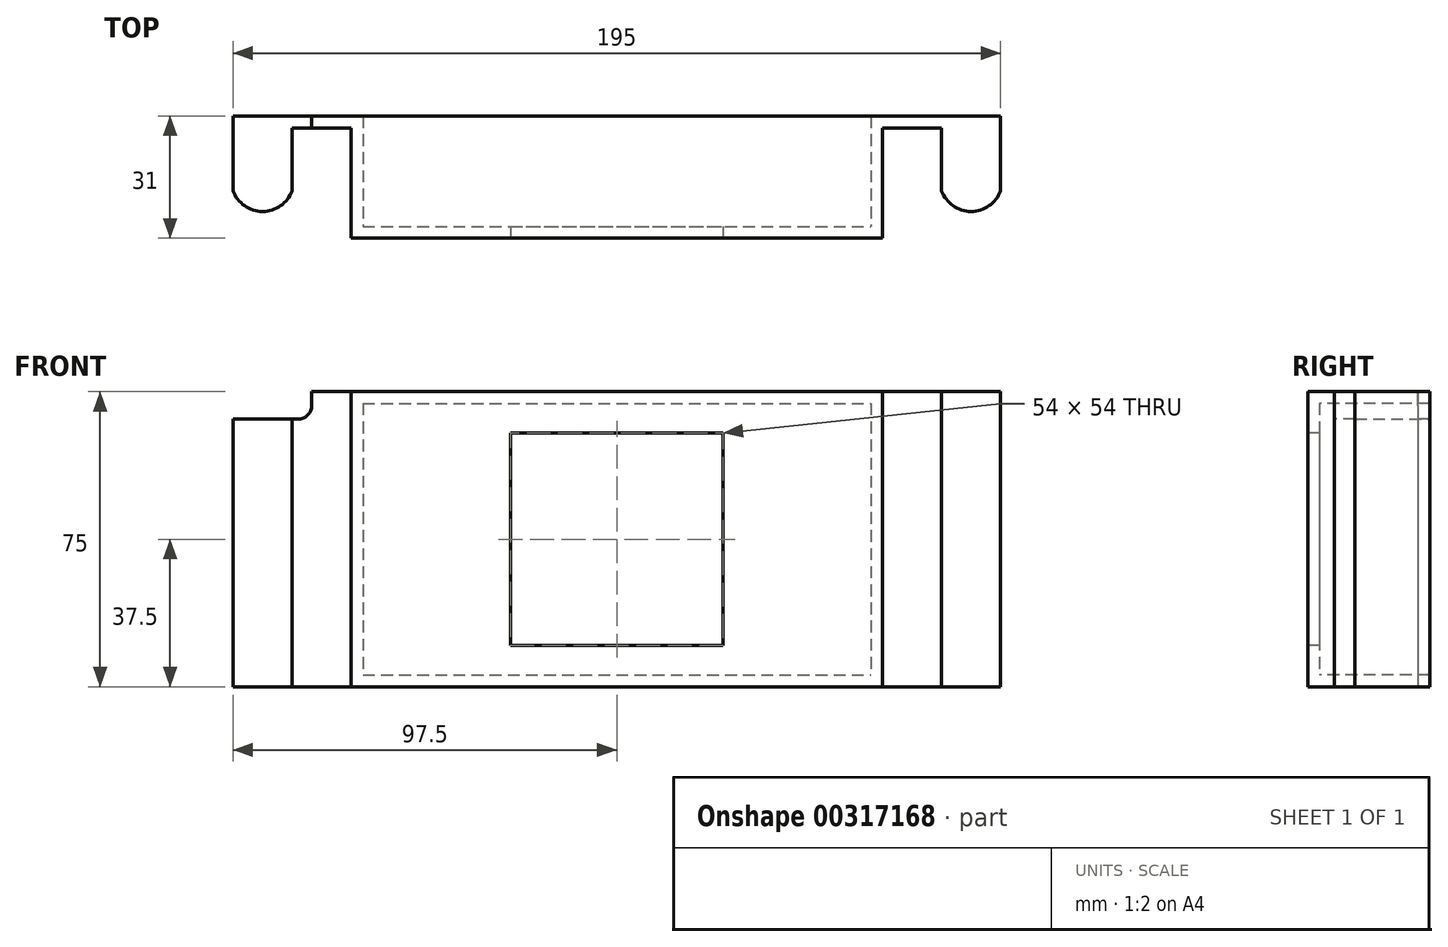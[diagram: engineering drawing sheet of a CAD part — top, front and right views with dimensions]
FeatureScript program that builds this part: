
annotation { "Feature Type Name" : "Feature", "Feature Type Description" : "" }
export const myFeature = defineFeature(function(context is Context, id is Id, definition is map)
    precondition{}
    {
        {
            var Q0;
            Q0=qCreatedBy(makeId("Front.planeOp"),FACE);
            var sketch = newSketch(context, id + "F0", { "sketchPlane" : qUnion([Q0])});
            skLineSegment(sketch, "E0.bottom", {"start": v(30, 30) * mm, "end": v(-30, 30) * mm});
            skLineSegment(sketch, "E0.top", {"start": v(30, -30) * mm, "end": v(-30, -30) * mm});
            skLineSegment(sketch, "E0.left", {"start": v(30, 30) * mm, "end": v(30, -30) * mm});
            skLineSegment(sketch, "E0.right", {"start": v(-30, 30) * mm, "end": v(-30, -30) * mm});
            skPoint(sketch, "E0.middle", {"position": v(0, 0) * mm});
            skCircle(sketch, "E1", {"center": v(0, 0) * mm, "radius": 22.4 * mm});
            skSolve(sketch);
        }
        {
            var Q0;
            Q0=qSketchRegion(id+"F0",true);
            extrude(context, id + "F1", {"entities" : qUnion([Q0]), "depth" : 3 * mm});
        }
        {
            var Q0;
            Q0=makeQuery(id+"F1.opExtrude","CAP_FACE",FACE,{"disambiguationData":[OSD([sQuery(id+"F0.wireOp",EDGE,"E0.bottom"),sQuery(id+"F0.wireOp",EDGE,"E0.top"),sQuery(id+"F0.wireOp",EDGE,"E0.left"),sQuery(id+"F0.wireOp",EDGE,"E0.right"),sQuery(id+"F0.wireOp",EDGE,"E1")])],"isStart":true});
            var sketch = newSketch(context, id + "F2", { "sketchPlane" : qUnion([Q0])});
            skLineSegment(sketch, "E2.bottom", {"start": v(30, 30) * mm, "end": v(-30, 30) * mm});
            skLineSegment(sketch, "E2.top", {"start": v(30, -30) * mm, "end": v(-30, -30) * mm});
            skLineSegment(sketch, "E2.left", {"start": v(30, 30) * mm, "end": v(30, -30) * mm});
            skLineSegment(sketch, "E2.right", {"start": v(-30, 30) * mm, "end": v(-30, -30) * mm});
            skPoint(sketch, "E2.middle", {"position": v(0, 0) * mm});
            skLineSegment(sketch, "E3.bottom", {"start": v(27, 27) * mm, "end": v(-27, 27) * mm});
            skLineSegment(sketch, "E3.top", {"start": v(27, -27) * mm, "end": v(-27, -27) * mm});
            skLineSegment(sketch, "E3.left", {"start": v(27, 27) * mm, "end": v(27, -27) * mm});
            skLineSegment(sketch, "E3.right", {"start": v(-27, 27) * mm, "end": v(-27, -27) * mm});
            skSolve(sketch);
        }
        {
            var Q0;
            Q0=qSketchRegion(id+"F2",true);
            extrude(context, id + "F3", {"entities" : qUnion([Q0]), "operationType" : NewBodyOperationType.ADD, "depth" : 15 * mm});
        }
        {
            var Q0;
            Q0=makeQuery(id+"F3.opExtrude","CAP_FACE",FACE,{"disambiguationData":[OSD([sQuery(id+"F2.wireOp",EDGE,"E2.bottom"),sQuery(id+"F2.wireOp",EDGE,"E2.top"),sQuery(id+"F2.wireOp",EDGE,"E2.left"),sQuery(id+"F2.wireOp",EDGE,"E2.right"),sQuery(id+"F2.wireOp",EDGE,"E3.bottom"),sQuery(id+"F2.wireOp",EDGE,"E3.top"),sQuery(id+"F2.wireOp",EDGE,"E3.left"),sQuery(id+"F2.wireOp",EDGE,"E3.right")])],"isStart":false});
            var sketch = newSketch(context, id + "F4", { "sketchPlane" : qUnion([Q0])});
            skLineSegment(sketch, "E4.bottom", {"start": v(67.5, 37.5) * mm, "end": v(-67.5, 37.5) * mm});
            skLineSegment(sketch, "E4.top", {"start": v(67.5, -37.5) * mm, "end": v(-67.5, -37.5) * mm});
            skLineSegment(sketch, "E4.left", {"start": v(67.5, 37.5) * mm, "end": v(67.5, -37.5) * mm});
            skLineSegment(sketch, "E4.right", {"start": v(-67.5, 37.5) * mm, "end": v(-67.5, -37.5) * mm});
            skPoint(sketch, "E4.middle", {"position": v(0, 0) * mm});
            skLineSegment(sketch, "E5.bottom", {"start": v(27, 27) * mm, "end": v(-27, 27) * mm});
            skLineSegment(sketch, "E5.top", {"start": v(27, -27) * mm, "end": v(-27, -27) * mm});
            skLineSegment(sketch, "E5.left", {"start": v(27, 27) * mm, "end": v(27, -27) * mm});
            skLineSegment(sketch, "E5.right", {"start": v(-27, 27) * mm, "end": v(-27, -27) * mm});
            skSolve(sketch);
        }
        {
            var Q0;
            Q0=qSketchRegion(id+"F4",true);
            extrude(context, id + "F5", {"entities" : qUnion([Q0]), "operationType" : NewBodyOperationType.ADD, "depth" : 3 * mm});
        }
        {
            var Q0;
            Q0=makeQuery(id+"F5.opExtrude","CAP_FACE",FACE,{"disambiguationData":[OSD([sQuery(id+"F4.wireOp",EDGE,"E4.bottom"),sQuery(id+"F4.wireOp",EDGE,"E4.top"),sQuery(id+"F4.wireOp",EDGE,"E4.left"),sQuery(id+"F4.wireOp",EDGE,"E4.right"),sQuery(id+"F4.wireOp",EDGE,"E5.bottom"),sQuery(id+"F4.wireOp",EDGE,"E5.top"),sQuery(id+"F4.wireOp",EDGE,"E5.left"),sQuery(id+"F4.wireOp",EDGE,"E5.right")])],"isStart":false});
            var sketch = newSketch(context, id + "F6", { "sketchPlane" : qUnion([Q0])});
            skLineSegment(sketch, "E6.bottom", {"start": v(67.5, 37.5) * mm, "end": v(-67.5, 37.5) * mm});
            skLineSegment(sketch, "E6.top", {"start": v(67.5, -37.5) * mm, "end": v(-67.5, -37.5) * mm});
            skLineSegment(sketch, "E6.left", {"start": v(67.5, 37.5) * mm, "end": v(67.5, -37.5) * mm});
            skLineSegment(sketch, "E6.right", {"start": v(-67.5, 37.5) * mm, "end": v(-67.5, -37.5) * mm});
            skPoint(sketch, "E6.middle", {"position": v(0, 0) * mm});
            skLineSegment(sketch, "E7.bottom", {"start": v(64.5, 34.5) * mm, "end": v(-64.5, 34.5) * mm});
            skLineSegment(sketch, "E7.top", {"start": v(64.5, -34.5) * mm, "end": v(-64.5, -34.5) * mm});
            skLineSegment(sketch, "E7.left", {"start": v(64.5, 34.5) * mm, "end": v(64.5, -34.5) * mm});
            skLineSegment(sketch, "E7.right", {"start": v(-64.5, 34.5) * mm, "end": v(-64.5, -34.5) * mm});
            skSolve(sketch);
        }
        {
            var Q0;
            Q0=qSketchRegion(id+"F6",true);
            extrude(context, id + "F7", {"entities" : qUnion([Q0]), "operationType" : NewBodyOperationType.ADD, "depth" : 25 * mm});
        }
        {
            var Q0;
            Q0=makeQuery(id+"F7.opExtrude","CAP_FACE",FACE,{"disambiguationData":[OSD([sQuery(id+"F6.wireOp",EDGE,"E6.bottom"),sQuery(id+"F6.wireOp",EDGE,"E6.top"),sQuery(id+"F6.wireOp",EDGE,"E6.left"),sQuery(id+"F6.wireOp",EDGE,"E6.right"),sQuery(id+"F6.wireOp",EDGE,"E7.bottom"),sQuery(id+"F6.wireOp",EDGE,"E7.top"),sQuery(id+"F6.wireOp",EDGE,"E7.left"),sQuery(id+"F6.wireOp",EDGE,"E7.right")])],"isStart":false});
            var sketch = newSketch(context, id + "F8", { "sketchPlane" : qUnion([Q0])});
            skLineSegment(sketch, "E8.bottom", {"start": v(97.5, 37.5) * mm, "end": v(-97.5, 37.5) * mm});
            skLineSegment(sketch, "E8.top", {"start": v(97.5, -37.5) * mm, "end": v(-97.5, -37.5) * mm});
            skLineSegment(sketch, "E8.left", {"start": v(97.5, 37.5) * mm, "end": v(97.5, -37.5) * mm});
            skLineSegment(sketch, "E8.right", {"start": v(-97.5, 37.5) * mm, "end": v(-97.5, -37.5) * mm});
            skPoint(sketch, "E8.middle", {"position": v(0, 0) * mm});
            skLineSegment(sketch, "E9.bottom", {"start": v(64.5, 34.5) * mm, "end": v(-64.5, 34.5) * mm});
            skLineSegment(sketch, "E9.top", {"start": v(64.5, -34.5) * mm, "end": v(-64.5, -34.5) * mm});
            skLineSegment(sketch, "E9.left", {"start": v(64.5, 34.5) * mm, "end": v(64.5, -34.5) * mm});
            skLineSegment(sketch, "E9.right", {"start": v(-64.5, 34.5) * mm, "end": v(-64.5, -34.5) * mm});
            skSolve(sketch);
        }
        {
            var Q0;
            Q0=qSketchRegion(id+"F8",true);
            extrude(context, id + "F9", {"entities" : qUnion([Q0]), "operationType" : NewBodyOperationType.ADD, "depth" : 3 * mm});
        }
        {
            var Q0;
            {var subQ0=sQuery(id+"F8.wireOp",EDGE,"E8.left");var subQ1=sQuery(id+"F8.wireOp",EDGE,"E8.bottom");var subQ2=sQuery(id+"F8.wireOp",EDGE,"E8.top");Q0=makeQuery(id+"F9.boolean.opBoolean","SPLIT",FACE,{"disambiguationData":[TD([makeQuery(id+"F5.opExtrude","SWEPT_FACE",FACE,{"disambiguationData":[OSD([sQuery(id+"F4.wireOp",EDGE,"E4.left")])]})])],"derivedFrom":makeQuery(id+"F9.opExtrude","CAP_FACE",FACE,{"disambiguationData":[OSD([subQ1,subQ2,subQ0,sQuery(id+"F8.wireOp",EDGE,"E8.right"),sQuery(id+"F8.wireOp",EDGE,"E9.bottom"),sQuery(id+"F8.wireOp",EDGE,"E9.top"),sQuery(id+"F8.wireOp",EDGE,"E9.left"),sQuery(id+"F8.wireOp",EDGE,"E9.right")])],"isStart":true})});}
            var sketch = newSketch(context, id + "F10", { "sketchPlane" : qUnion([Q0])});
            skLineSegment(sketch, "E10.top", {"start": v(-97.5, -37.5) * mm, "end": v(-82.5, -37.5) * mm});
            skLineSegment(sketch, "E11", {"start": v(-97.5, 30.5) * mm, "end": v(-82.5, 30.5) * mm});
            skLineSegment(sketch, "E12", {"start": v(-82.5, 30.5) * mm, "end": v(-82.5, -37.5) * mm});
            skLineSegment(sketch, "E13", {"start": v(-97.5, -37.5) * mm, "end": v(-97.5, 30.5) * mm});
            skSolve(sketch);
        }
        {
            var Q0;
            Q0=qSketchRegion(id+"F10",true);
            extrude(context, id + "F11", {"entities" : qUnion([Q0]), "operationType" : NewBodyOperationType.ADD, "depth" : 25 * mm});
        }
        {
            var Q0;
            {var subQ0=sQuery(id+"F8.wireOp",EDGE,"E8.bottom");var subQ1=sQuery(id+"F8.wireOp",EDGE,"E8.top");var subQ2=sQuery(id+"F8.wireOp",EDGE,"E8.right");Q0=makeQuery(id+"F9.boolean.opBoolean","SPLIT",FACE,{"disambiguationData":[TD([makeQuery(id+"F5.opExtrude","SWEPT_FACE",FACE,{"disambiguationData":[OSD([sQuery(id+"F4.wireOp",EDGE,"E4.right")])]})])],"derivedFrom":makeQuery(id+"F9.opExtrude","CAP_FACE",FACE,{"disambiguationData":[OSD([subQ0,subQ1,sQuery(id+"F8.wireOp",EDGE,"E8.left"),subQ2,sQuery(id+"F8.wireOp",EDGE,"E9.bottom"),sQuery(id+"F8.wireOp",EDGE,"E9.top"),sQuery(id+"F8.wireOp",EDGE,"E9.left"),sQuery(id+"F8.wireOp",EDGE,"E9.right")])],"isStart":true})});}
            var sketch = newSketch(context, id + "F12", { "sketchPlane" : qUnion([Q0])});
            skLineSegment(sketch, "E14.bottom", {"start": v(97.5, 37.5) * mm, "end": v(82.5, 37.5) * mm});
            skLineSegment(sketch, "E14.top", {"start": v(97.5, -37.5) * mm, "end": v(82.5, -37.5) * mm});
            skLineSegment(sketch, "E14.left", {"start": v(97.5, 37.5) * mm, "end": v(97.5, -37.5) * mm});
            skLineSegment(sketch, "E14.right", {"start": v(82.5, 37.5) * mm, "end": v(82.5, -37.5) * mm});
            skSolve(sketch);
        }
        {
            var Q0;
            Q0=qSketchRegion(id+"F12",true);
            extrude(context, id + "F13", {"entities" : qUnion([Q0]), "operationType" : NewBodyOperationType.ADD, "depth" : 25 * mm});
        }
        {
            var Q0;
            Q0=makeQuery(id+"F13.boolean.opBoolean","MERGE",FACE,{"derivedFrom":[makeQuery(id+"F11.boolean.opBoolean","MERGE",FACE,{"derivedFrom":[makeQuery(id+"F9.boolean.opBoolean","MERGE",FACE,{"derivedFrom":[makeQuery(id+"F7.boolean.opBoolean","MERGE",FACE,{"derivedFrom":[makeQuery(id+"F5.opExtrude","SWEPT_FACE",FACE,{"disambiguationData":[OSD([sQuery(id+"F4.wireOp",EDGE,"E4.bottom")])]}),makeQuery(id+"F7.opExtrude","SWEPT_FACE",FACE,{"disambiguationData":[OSD([sQuery(id+"F6.wireOp",EDGE,"E6.bottom")])]})]}),makeQuery(id+"F9.opExtrude","SWEPT_FACE",FACE,{"disambiguationData":[OSD([sQuery(id+"F8.wireOp",EDGE,"E8.bottom")])]})]}),makeQuery(id+"F11.opExtrude","SWEPT_FACE",FACE,{"disambiguationData":[OSD([sQuery(id+"F10.wireOp",EDGE,"E10.bottom")])]})]}),makeQuery(id+"F13.opExtrude","SWEPT_FACE",FACE,{"disambiguationData":[OSD([sQuery(id+"F12.wireOp",EDGE,"E14.bottom")])]})]});
            var sketch = newSketch(context, id + "F14", { "sketchPlane" : qUnion([Q0])});
            skArc(sketch, "E15", {"start": v(-97.5, 27) * mm, "mid": v(-90, 21.78) * mm, "end": v(-82.5, 27) * mm});
            skArc(sketch, "E16", {"start": v(82.5, 27) * mm, "mid": v(90, 21.78) * mm, "end": v(97.5, 27) * mm});
            skLineSegment(sketch, "E17", {"start": v(-97.5, 27) * mm, "end": v(-97.5, 18) * mm});
            skLineSegment(sketch, "E18", {"start": v(-97.5, 18) * mm, "end": v(-82.5, 18) * mm});
            skLineSegment(sketch, "E19", {"start": v(-82.5, 18) * mm, "end": v(-82.5, 27) * mm});
            skLineSegment(sketch, "E20", {"start": v(82.5, 27) * mm, "end": v(82.5, 18) * mm});
            skLineSegment(sketch, "E21", {"start": v(82.5, 18) * mm, "end": v(97.5, 18) * mm});
            skLineSegment(sketch, "E22", {"start": v(97.5, 18) * mm, "end": v(97.5, 27) * mm});
            skSolve(sketch);
        }
        {
            var Q0;
            Q0=qSketchRegion(id+"F14",true);
            extrude(context, id + "F15", {"entities" : qUnion([Q0]), "operationType" : NewBodyOperationType.REMOVE, "oppositeDirection" : true, "depth" : 200 * mm});
        }
        {
            var Q0;
            {var subQ0=sQuery(id+"F8.wireOp",EDGE,"E8.left");var subQ1=sQuery(id+"F8.wireOp",EDGE,"E8.bottom");var subQ2=sQuery(id+"F8.wireOp",EDGE,"E8.top");Q0=makeQuery(id+"F9.boolean.opBoolean","SPLIT",FACE,{"disambiguationData":[TD([makeQuery(id+"F5.opExtrude","SWEPT_FACE",FACE,{"disambiguationData":[OSD([sQuery(id+"F4.wireOp",EDGE,"E4.left")])]})])],"derivedFrom":makeQuery(id+"F9.opExtrude","CAP_FACE",FACE,{"disambiguationData":[OSD([subQ1,subQ2,subQ0,sQuery(id+"F8.wireOp",EDGE,"E8.right"),sQuery(id+"F8.wireOp",EDGE,"E9.bottom"),sQuery(id+"F8.wireOp",EDGE,"E9.top"),sQuery(id+"F8.wireOp",EDGE,"E9.left"),sQuery(id+"F8.wireOp",EDGE,"E9.right")])],"isStart":true})});}
            var sketch = newSketch(context, id + "F16", { "sketchPlane" : qUnion([Q0])});
            skLineSegment(sketch, "E23", {"start": v(-82.5, 37.5) * mm, "end": v(-97.5, 37.5) * mm});
            skLineSegment(sketch, "E24", {"start": v(-97.5, 37.5) * mm, "end": v(-97.5, 30.5) * mm});
            skLineSegment(sketch, "E25", {"start": v(-97.5, 30.5) * mm, "end": v(-97.5, 37.5) * mm});
            skLineSegment(sketch, "E26", {"start": v(-82.5, 30.5) * mm, "end": v(-97.5, 30.5) * mm});
            skLineSegment(sketch, "E27", {"start": v(-82.5, 30.5) * mm, "end": v(-77.5, 30.5) * mm});
            skLineSegment(sketch, "E28", {"start": v(-77.5, 30.5) * mm, "end": v(-77.5, 37.5) * mm});
            skLineSegment(sketch, "E29", {"start": v(-77.5, 37.5) * mm, "end": v(-82.5, 37.5) * mm});
            skSolve(sketch);
        }
        {
            var Q0;
            Q0=qSketchRegion(id+"F16",true);
            extrude(context, id + "F17", {"entities" : qUnion([Q0]), "operationType" : NewBodyOperationType.REMOVE, "oppositeDirection" : true, "depth" : 25 * mm});
        }
        {
            var Q0;
            Q0=makeQuery(id+"F17.boolean.opBoolean","COPY",EDGE,{"derivedFrom":makeQuery(id+"F17.opExtrude","SWEPT_EDGE",EDGE,{"disambiguationData":[OSD([sQuery(id+"F16.wireOp",EDGE,"E27"),sQuery(id+"F16.wireOp",EDGE,"E28")])]})});
            var Q1;
            Q1=makeQuery(id+"F17.boolean.opBoolean","COPY",EDGE,{"derivedFrom":makeQuery(id+"F17.opExtrude","SWEPT_EDGE",EDGE,{"disambiguationData":[OSD([sQuery(id+"F8.wireOp",EDGE,"E8.bottom"),sQuery(id+"F16.wireOp",EDGE,"E28"),sQuery(id+"F16.wireOp",EDGE,"E29")])]})});
            fillet(context, id + "F18", {"entities" : qUnion([Q0, Q1]), "radius" : 3.5 * mm, "tangentPropagation" : true, "allowEdgeOverflow" : false});
        }
        {
            var Q0;
            Q0=makeQuery(id+"F19.boolean.opBoolean","MERGE",FACE,{"derivedFrom":[makeQuery(id+"F3.boolean.opBoolean","MERGE",FACE,{"derivedFrom":[makeQuery(id+"F1.opExtrude","SWEPT_FACE",FACE,{"disambiguationData":[OSD([sQuery(id+"F0.wireOp",EDGE,"E0.bottom")])]}),makeQuery(id+"F3.opExtrude","SWEPT_FACE",FACE,{"disambiguationData":[OSD([sQuery(id+"F2.wireOp",EDGE,"E2.bottom")])]})]}),makeQuery(id+"F19.opExtrude","SWEPT_FACE",FACE,{"disambiguationData":[OSD([sQuery(id+"Fg7M6V97ZkYJ0yG_1.wireOp",EDGE,"ihL5YEDn-t8Oy-xYXL-v36N-uPn2xZnvlxlS.bottom")])]})]});
            var sketch = newSketch(context, id + "F20", { "sketchPlane" : qUnion([Q0])});
            skLineSegment(sketch, "E30", {"start": v(-50, 15) * mm, "end": v(-30, -3) * mm});
            skLineSegment(sketch, "E31", {"start": v(-30, -3) * mm, "end": v(-50, -3) * mm});
            skLineSegment(sketch, "E32", {"start": v(-50, -3) * mm, "end": v(-50, 15) * mm});
            skSolve(sketch);
        }
        {
            var Q0;
            Q0=qSketchRegion(id+"F20",true);
            extrude(context, id + "F21", {"entities" : qUnion([Q0]), "operationType" : NewBodyOperationType.REMOVE, "oppositeDirection" : true, "depth" : 60 * mm});
        }
        {
            var Q0;
            Q0=makeQuery(id+"F1.opExtrude","CAP_FACE",FACE,{"disambiguationData":[OSD([sQuery(id+"F0.wireOp",EDGE,"E0.bottom"),sQuery(id+"F0.wireOp",EDGE,"E0.top"),sQuery(id+"F0.wireOp",EDGE,"E0.left"),sQuery(id+"F0.wireOp",EDGE,"E0.right"),sQuery(id+"F0.wireOp",EDGE,"E1")])],"isStart":false});
            var sketch = newSketch(context, id + "F24", { "sketchPlane" : qUnion([Q0])});
            skLineSegment(sketch, "E33.bottom", {"start": v(-30, 30) * mm, "end": v(30, 30) * mm});
            skLineSegment(sketch, "E33.top", {"start": v(-30, -30) * mm, "end": v(30, -30) * mm});
            skLineSegment(sketch, "E33.left", {"start": v(-30, 30) * mm, "end": v(-30, -30) * mm});
            skLineSegment(sketch, "E33.right", {"start": v(30, 30) * mm, "end": v(30, -30) * mm});
            skSolve(sketch);
        }
        {
            var Q0;
            Q0 = qSketchRegion(id + "F24", true);
            extrude(context, id + "F25", {"entities" : qUnion([Q0]), "operationType" : NewBodyOperationType.REMOVE, "oppositeDirection" : true, "depth" : 18 * mm});
        }
    });
